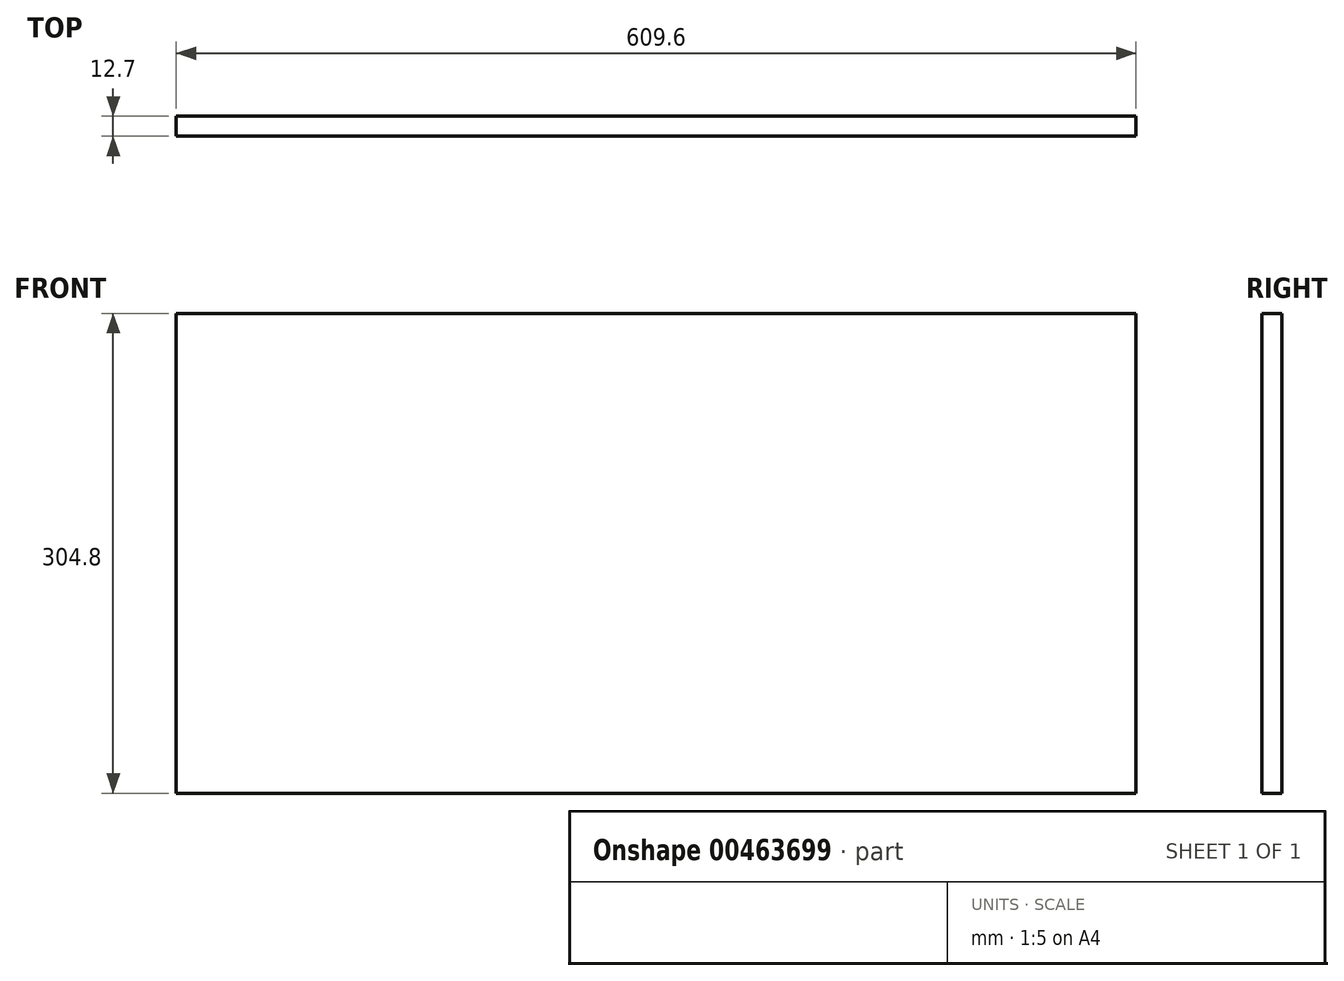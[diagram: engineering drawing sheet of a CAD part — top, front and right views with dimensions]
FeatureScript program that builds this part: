
annotation { "Feature Type Name" : "Feature", "Feature Type Description" : "" }
export const myFeature = defineFeature(function(context is Context, id is Id, definition is map)
    precondition{}
    {
        {
            var Q0;
            Q0=qCreatedBy(makeId("Front.planeOp"),FACE);
            var sketch = newSketch(context, id + "F0", { "sketchPlane" : qUnion([Q0])});
            skLineSegment(sketch, "E0.bottom", {"start": v(-303.7, 168.12) * mm, "end": v(305.9, 168.12) * mm});
            skLineSegment(sketch, "E0.top", {"start": v(-303.7, -136.68) * mm, "end": v(305.9, -136.68) * mm});
            skLineSegment(sketch, "E0.left", {"start": v(-303.7, 168.12) * mm, "end": v(-303.7, -136.68) * mm});
            skLineSegment(sketch, "E0.right", {"start": v(305.9, 168.12) * mm, "end": v(305.9, -136.68) * mm});
            skSolve(sketch);
        }
        {
            var Q0;
            Q0 = qSketchRegion(id + "F0", true);
            extrude(context, id + "F1", {"entities" : qUnion([Q0]), "depth" : 12.7 * mm});
        }
    });
